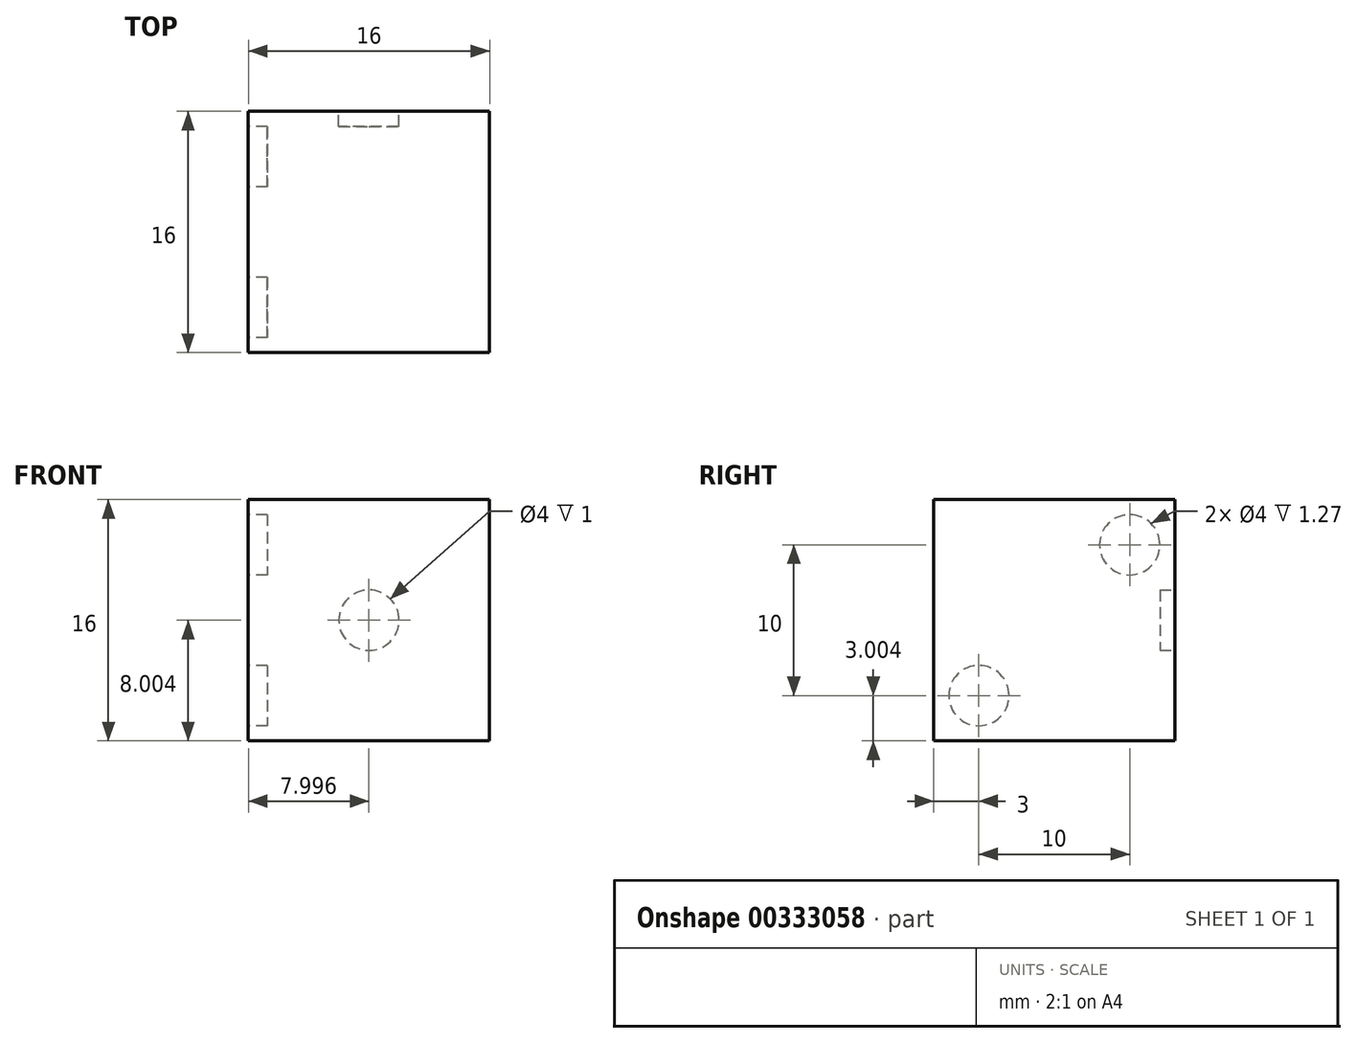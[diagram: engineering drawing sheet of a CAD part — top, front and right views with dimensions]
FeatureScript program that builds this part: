
annotation { "Feature Type Name" : "Feature", "Feature Type Description" : "" }
export const myFeature = defineFeature(function(context is Context, id is Id, definition is map)
    precondition{}
    {
        {
            var Q0;
            Q0=qCreatedBy(makeId("Front.planeOp"),FACE);
            var sketch = newSketch(context, id + "F0", { "sketchPlane" : qUnion([Q0])});
            skLineSegment(sketch, "E0.bottom", {"start": v(-32.35, 3.9) * mm, "end": v(-16.35, 3.9) * mm});
            skLineSegment(sketch, "E0.top", {"start": v(-32.35, -12.1) * mm, "end": v(-16.35, -12.1) * mm});
            skLineSegment(sketch, "E0.left", {"start": v(-32.35, 3.9) * mm, "end": v(-32.35, -12.1) * mm});
            skLineSegment(sketch, "E0.right", {"start": v(-16.35, 3.9) * mm, "end": v(-16.35, -12.1) * mm});
            skSolve(sketch);
        }
        {
            var Q0;
            Q0=makeQuery(id+"F0.imprint","IMPRINT",FACE,{"disambiguationData":[TD([[makeQuery(id+"F0.imprint","IMPRINT",EDGE,{"derivedFrom":sQuery(id+"F0.wireOp",EDGE,"E0.bottom")}),-1.0]])]});
            extrude(context, id + "F1", {"entities" : qUnion([Q0]), "depth" : 16 * mm});
        }
        {
            var Q0;
            Q0=makeQuery(id+"F1.opExtrude","CAP_FACE",FACE,{"disambiguationData":[OSD([sQuery(id+"F0.wireOp",EDGE,"E0.bottom"),sQuery(id+"F0.wireOp",EDGE,"E0.top"),sQuery(id+"F0.wireOp",EDGE,"E0.left"),sQuery(id+"F0.wireOp",EDGE,"E0.right")])],"isStart":true});
            var sketch = newSketch(context, id + "F2", { "sketchPlane" : qUnion([Q0])});
            skCircle(sketch, "E1", {"center": v(24.35, -4.1) * mm, "radius": 2 * mm});
            skSolve(sketch);
        }
        {
            var Q0;
            Q0 = qSketchRegion(id + "F2", true);
            extrude(context, id + "F3", {"entities" : qUnion([Q0]), "operationType" : NewBodyOperationType.REMOVE, "oppositeDirection" : true, "depth" : 1 * mm});
        }
        {
            var Q0;
            Q0=makeQuery(id+"F1.opExtrude","SWEPT_FACE",FACE,{"disambiguationData":[OSD([sQuery(id+"F0.wireOp",EDGE,"E0.left")])]});
            var sketch = newSketch(context, id + "F4", { "sketchPlane" : qUnion([Q0])});
            skCircle(sketch, "E2", {"center": v(13, -9.1) * mm, "radius": 2 * mm});
            skCircle(sketch, "E3", {"center": v(3, 0.9) * mm, "radius": 2 * mm});
            skSolve(sketch);
        }
        {
            var Q0;
            Q0=makeQuery(id+"F1.opExtrude","SWEPT_FACE",FACE,{"disambiguationData":[OSD([sQuery(id+"F0.wireOp",EDGE,"E0.right")])]});
            var sketch = newSketch(context, id + "F5", { "sketchPlane" : qUnion([Q0])});
            skCircle(sketch, "E4", {"center": v(-12, -0.1) * mm, "radius": 2 * mm});
            skCircle(sketch, "E5", {"center": v(-4, -0.1) * mm, "radius": 2 * mm});
            skCircle(sketch, "E6", {"center": v(-8, -4.1) * mm, "radius": 2 * mm});
            skCircle(sketch, "E7", {"center": v(-12, -8.1) * mm, "radius": 2 * mm});
            skCircle(sketch, "E8", {"center": v(-4, -8.1) * mm, "radius": 2 * mm});
            skSolve(sketch);
        }
        {
            var Q0;
            Q0 = qSketchRegion(id + "F4", true);
            extrude(context, id + "F6", {"entities" : qUnion([Q0]), "operationType" : NewBodyOperationType.REMOVE, "oppositeDirection" : true, "depth" : 1.27 * mm});
        }
    });
